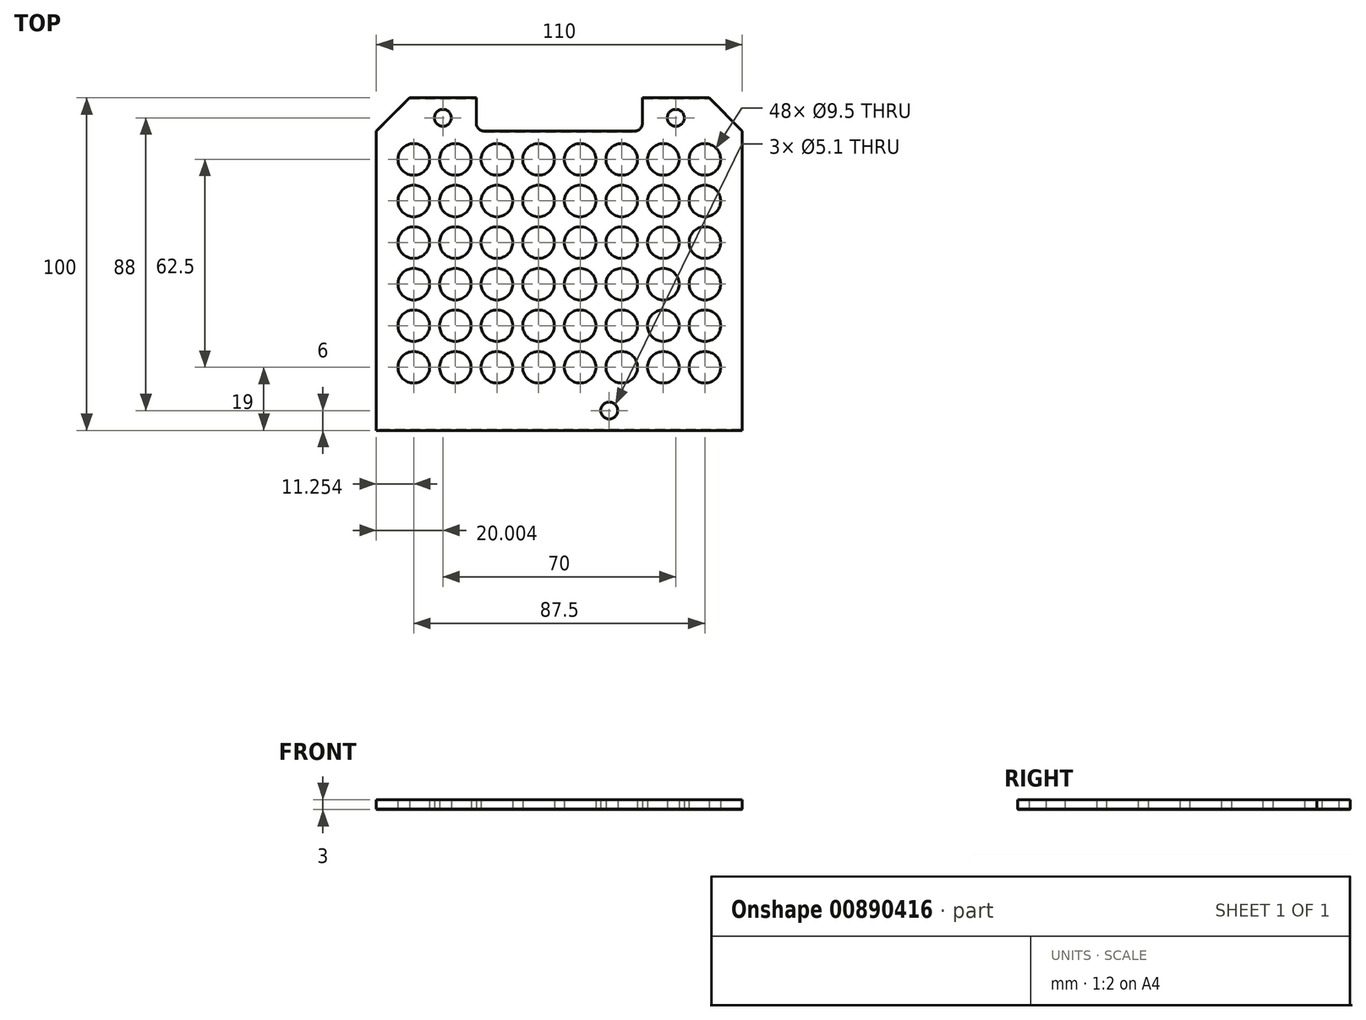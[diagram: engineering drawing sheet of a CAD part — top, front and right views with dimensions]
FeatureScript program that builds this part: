
annotation { "Feature Type Name" : "Feature", "Feature Type Description" : "" }
export const myFeature = defineFeature(function(context is Context, id is Id, definition is map)
    precondition{}
    {
        {
            var Q0;
            Q0=qCreatedBy(makeId("Top.planeOp"),FACE);
            var sketch = newSketch(context, id + "F0", { "sketchPlane" : qUnion([Q0])});
            skLineSegment(sketch, "E0", {"start": v(-42.4, 0) * mm, "end": v(67.6, 0) * mm});
            skLineSegment(sketch, "E1", {"start": v(-42.4, 100) * mm, "end": v(67.6, 100) * mm, "construction": true});
            skLineSegment(sketch, "E2", {"start": v(-42.4, 0) * mm, "end": v(-42.4, 100) * mm, "construction": true});
            skLineSegment(sketch, "E3", {"start": v(67.6, 0) * mm, "end": v(67.6, 100) * mm, "construction": true});
            skLineSegment(sketch, "E4", {"start": v(-12.4, 100) * mm, "end": v(-12.4, 90) * mm});
            skLineSegment(sketch, "E5", {"start": v(-12.4, 90) * mm, "end": v(37.6, 90) * mm});
            skLineSegment(sketch, "E6", {"start": v(37.6, 90) * mm, "end": v(37.6, 100) * mm});
            skLineSegment(sketch, "E7", {"start": v(-12.4, 100) * mm, "end": v(-32.4, 100) * mm});
            skLineSegment(sketch, "E8", {"start": v(-32.4, 100) * mm, "end": v(-42.4, 90) * mm});
            skLineSegment(sketch, "E9", {"start": v(-42.4, 90) * mm, "end": v(-42.4, 0) * mm});
            skLineSegment(sketch, "E10", {"start": v(37.6, 100) * mm, "end": v(57.6, 100) * mm});
            skLineSegment(sketch, "E11", {"start": v(57.6, 100) * mm, "end": v(67.6, 90) * mm});
            skLineSegment(sketch, "E12", {"start": v(67.6, 90) * mm, "end": v(67.6, 0) * mm});
            skLineSegment(sketch, "E13", {"start": v(-42.4, 19) * mm, "end": v(67.6, 19) * mm, "construction": true});
            skCircle(sketch, "E14", {"center": v(-31.16, 19) * mm, "radius": 4.75 * mm});
            skCircle(sketch, "E15.0.1.0", {"center": v(-31.16, 31.5) * mm, "radius": 4.75 * mm});
            skCircle(sketch, "E15.0.2.0", {"center": v(-31.16, 44) * mm, "radius": 4.75 * mm});
            skCircle(sketch, "E15.0.3.0", {"center": v(-31.16, 56.5) * mm, "radius": 4.75 * mm});
            skCircle(sketch, "E15.0.4.0", {"center": v(-31.16, 69) * mm, "radius": 4.75 * mm});
            skCircle(sketch, "E15.0.5.0", {"center": v(-31.16, 81.5) * mm, "radius": 4.75 * mm});
            skCircle(sketch, "E15.1.0.0", {"center": v(-18.66, 19) * mm, "radius": 4.75 * mm});
            skCircle(sketch, "E15.1.1.0", {"center": v(-18.66, 31.5) * mm, "radius": 4.75 * mm});
            skCircle(sketch, "E15.1.2.0", {"center": v(-18.66, 44) * mm, "radius": 4.75 * mm});
            skCircle(sketch, "E15.1.3.0", {"center": v(-18.66, 56.5) * mm, "radius": 4.75 * mm});
            skCircle(sketch, "E15.1.4.0", {"center": v(-18.66, 69) * mm, "radius": 4.75 * mm});
            skCircle(sketch, "E15.1.5.0", {"center": v(-18.66, 81.5) * mm, "radius": 4.75 * mm});
            skCircle(sketch, "E15.2.0.0", {"center": v(-6.16, 19) * mm, "radius": 4.75 * mm});
            skCircle(sketch, "E15.2.1.0", {"center": v(-6.16, 31.5) * mm, "radius": 4.75 * mm});
            skCircle(sketch, "E15.2.2.0", {"center": v(-6.16, 44) * mm, "radius": 4.75 * mm});
            skCircle(sketch, "E15.2.3.0", {"center": v(-6.16, 56.5) * mm, "radius": 4.75 * mm});
            skCircle(sketch, "E15.2.4.0", {"center": v(-6.16, 69) * mm, "radius": 4.75 * mm});
            skCircle(sketch, "E15.2.5.0", {"center": v(-6.16, 81.5) * mm, "radius": 4.75 * mm});
            skCircle(sketch, "E15.3.0.0", {"center": v(6.34, 19) * mm, "radius": 4.75 * mm});
            skCircle(sketch, "E15.3.1.0", {"center": v(6.34, 31.5) * mm, "radius": 4.75 * mm});
            skCircle(sketch, "E15.3.2.0", {"center": v(6.34, 44) * mm, "radius": 4.75 * mm});
            skCircle(sketch, "E15.3.3.0", {"center": v(6.34, 56.5) * mm, "radius": 4.75 * mm});
            skCircle(sketch, "E15.3.4.0", {"center": v(6.34, 69) * mm, "radius": 4.75 * mm});
            skCircle(sketch, "E15.3.5.0", {"center": v(6.34, 81.5) * mm, "radius": 4.75 * mm});
            skCircle(sketch, "E15.4.0.0", {"center": v(18.84, 19) * mm, "radius": 4.75 * mm});
            skCircle(sketch, "E15.4.1.0", {"center": v(18.84, 31.5) * mm, "radius": 4.75 * mm});
            skCircle(sketch, "E15.4.2.0", {"center": v(18.84, 44) * mm, "radius": 4.75 * mm});
            skCircle(sketch, "E15.4.3.0", {"center": v(18.84, 56.5) * mm, "radius": 4.75 * mm});
            skCircle(sketch, "E15.4.4.0", {"center": v(18.84, 69) * mm, "radius": 4.75 * mm});
            skCircle(sketch, "E15.4.5.0", {"center": v(18.84, 81.5) * mm, "radius": 4.75 * mm});
            skCircle(sketch, "E15.5.0.0", {"center": v(31.34, 19) * mm, "radius": 4.75 * mm});
            skCircle(sketch, "E15.5.1.0", {"center": v(31.34, 31.5) * mm, "radius": 4.75 * mm});
            skCircle(sketch, "E15.5.2.0", {"center": v(31.34, 44) * mm, "radius": 4.75 * mm});
            skCircle(sketch, "E15.5.3.0", {"center": v(31.34, 56.5) * mm, "radius": 4.75 * mm});
            skCircle(sketch, "E15.5.4.0", {"center": v(31.34, 69) * mm, "radius": 4.75 * mm});
            skCircle(sketch, "E15.5.5.0", {"center": v(31.34, 81.5) * mm, "radius": 4.75 * mm});
            skCircle(sketch, "E15.6.0.0", {"center": v(43.84, 19) * mm, "radius": 4.75 * mm});
            skCircle(sketch, "E15.6.1.0", {"center": v(43.84, 31.5) * mm, "radius": 4.75 * mm});
            skCircle(sketch, "E15.6.2.0", {"center": v(43.84, 44) * mm, "radius": 4.75 * mm});
            skCircle(sketch, "E15.6.3.0", {"center": v(43.84, 56.5) * mm, "radius": 4.75 * mm});
            skCircle(sketch, "E15.6.4.0", {"center": v(43.84, 69) * mm, "radius": 4.75 * mm});
            skCircle(sketch, "E15.6.5.0", {"center": v(43.84, 81.5) * mm, "radius": 4.75 * mm});
            skCircle(sketch, "E15.7.0.0", {"center": v(56.34, 19) * mm, "radius": 4.75 * mm});
            skCircle(sketch, "E15.7.1.0", {"center": v(56.34, 31.5) * mm, "radius": 4.75 * mm});
            skCircle(sketch, "E15.7.2.0", {"center": v(56.34, 44) * mm, "radius": 4.75 * mm});
            skCircle(sketch, "E15.7.3.0", {"center": v(56.34, 56.5) * mm, "radius": 4.75 * mm});
            skCircle(sketch, "E15.7.4.0", {"center": v(56.34, 69) * mm, "radius": 4.75 * mm});
            skCircle(sketch, "E15.7.5.0", {"center": v(56.34, 81.5) * mm, "radius": 4.75 * mm});
            skLineSegment(sketch, "E15.direction1", {"start": v(-31.16, 19) * mm, "end": v(-18.66, 19) * mm, "construction": true});
            skLineSegment(sketch, "E15.direction2", {"start": v(-31.16, 19) * mm, "end": v(-31.16, 31.5) * mm, "construction": true});
            skCircle(sketch, "E16", {"center": v(27.6, 6) * mm, "radius": 2.55 * mm});
            skCircle(sketch, "E17", {"center": v(47.6, 94) * mm, "radius": 2.55 * mm});
            skCircle(sketch, "E18", {"center": v(-22.4, 94) * mm, "radius": 2.55 * mm});
            skSolve(sketch);
        }
        {
            var Q0;
            Q0 = qSketchRegion(id + "F0", true);
            extrude(context, id + "F1", {"entities" : qUnion([Q0]), "depth" : 3 * mm, "offsetDistance" : 25 * mm});
        }
        {
            var Q0;
            Q0=makeQuery(id+"F1.opExtrude","SWEPT_EDGE",EDGE,{"disambiguationData":[OSD([sQuery(id+"F0.wireOp",EDGE,"E4"),sQuery(id+"F0.wireOp",EDGE,"E5")])]});
            var Q1;
            Q1=makeQuery(id+"F1.opExtrude","SWEPT_EDGE",EDGE,{"disambiguationData":[OSD([sQuery(id+"F0.wireOp",EDGE,"E5"),sQuery(id+"F0.wireOp",EDGE,"E6")])]});
            fillet(context, id + "F2", {"entities" : qUnion([Q0, Q1]), "radius" : 2.5 * mm, "tangentPropagation" : true, "allowEdgeOverflow" : false});
        }
        {
            var Q0;
            Q0=makeQuery(id+"F1.opExtrude","CAP_EDGE",EDGE,{"disambiguationData":[OSD([sQuery(id+"F0.wireOp",EDGE,"E0")])],"isStart":true});
            var Q1;
            Q1=makeQuery(id+"F1.opExtrude","CAP_EDGE",EDGE,{"disambiguationData":[OSD([sQuery(id+"F0.wireOp",EDGE,"E12")])],"isStart":true});
            var Q2;
            Q2=makeQuery(id+"F1.opExtrude","CAP_EDGE",EDGE,{"disambiguationData":[OSD([sQuery(id+"F0.wireOp",EDGE,"E9")])],"isStart":true});
            var Q3;
            Q3=makeQuery(id+"F1.opExtrude","CAP_EDGE",EDGE,{"disambiguationData":[OSD([sQuery(id+"F0.wireOp",EDGE,"E11")])],"isStart":true});
            var Q4;
            Q4=makeQuery(id+"F1.opExtrude","CAP_EDGE",EDGE,{"disambiguationData":[OSD([sQuery(id+"F0.wireOp",EDGE,"E10")])],"isStart":true});
            var Q5;
            Q5=makeQuery(id+"F1.opExtrude","CAP_EDGE",EDGE,{"disambiguationData":[OSD([sQuery(id+"F0.wireOp",EDGE,"E4")])],"isStart":true});
            var Q6;
            Q6=makeQuery(id+"F1.opExtrude","CAP_EDGE",EDGE,{"disambiguationData":[OSD([sQuery(id+"F0.wireOp",EDGE,"E7")])],"isStart":true});
            var Q7;
            Q7=makeQuery(id+"F1.opExtrude","CAP_EDGE",EDGE,{"disambiguationData":[OSD([sQuery(id+"F0.wireOp",EDGE,"E8")])],"isStart":true});
            var Q8;
            {var subQ0=sQuery(id+"F0.wireOp",EDGE,"E5");var subQ1=sQuery(id+"F0.wireOp",EDGE,"E4");Q8=makeQuery(id+"F2.opFillet","BLEND_EDGE",EDGE,{"blendedFrom":[makeQuery(id+"F1.opExtrude","SWEPT_EDGE",EDGE,{"disambiguationData":[OSD([subQ1,subQ0])]}),makeQuery(id+"F1.opExtrude","CAP_FACE",FACE,{"disambiguationData":[OSD([sQuery(id+"F0.wireOp",EDGE,"E0"),subQ1,subQ0,sQuery(id+"F0.wireOp",EDGE,"E6"),sQuery(id+"F0.wireOp",EDGE,"E7"),sQuery(id+"F0.wireOp",EDGE,"E8"),sQuery(id+"F0.wireOp",EDGE,"E9"),sQuery(id+"F0.wireOp",EDGE,"E10"),sQuery(id+"F0.wireOp",EDGE,"E11"),sQuery(id+"F0.wireOp",EDGE,"E12"),sQuery(id+"F0.wireOp",EDGE,"E14"),sQuery(id+"F0.wireOp",EDGE,"E15.0.1.0"),sQuery(id+"F0.wireOp",EDGE,"E15.0.2.0"),sQuery(id+"F0.wireOp",EDGE,"E15.0.3.0"),sQuery(id+"F0.wireOp",EDGE,"E15.0.4.0"),sQuery(id+"F0.wireOp",EDGE,"E15.0.5.0"),sQuery(id+"F0.wireOp",EDGE,"E15.1.0.0"),sQuery(id+"F0.wireOp",EDGE,"E15.1.1.0"),sQuery(id+"F0.wireOp",EDGE,"E15.1.2.0"),sQuery(id+"F0.wireOp",EDGE,"E15.1.3.0"),sQuery(id+"F0.wireOp",EDGE,"E15.1.4.0"),sQuery(id+"F0.wireOp",EDGE,"E15.1.5.0"),sQuery(id+"F0.wireOp",EDGE,"E15.2.0.0"),sQuery(id+"F0.wireOp",EDGE,"E15.2.1.0"),sQuery(id+"F0.wireOp",EDGE,"E15.2.2.0"),sQuery(id+"F0.wireOp",EDGE,"E15.2.3.0"),sQuery(id+"F0.wireOp",EDGE,"E15.2.4.0"),sQuery(id+"F0.wireOp",EDGE,"E15.2.5.0"),sQuery(id+"F0.wireOp",EDGE,"E15.3.0.0"),sQuery(id+"F0.wireOp",EDGE,"E15.3.1.0"),sQuery(id+"F0.wireOp",EDGE,"E15.3.2.0"),sQuery(id+"F0.wireOp",EDGE,"E15.3.3.0"),sQuery(id+"F0.wireOp",EDGE,"E15.3.4.0"),sQuery(id+"F0.wireOp",EDGE,"E15.3.5.0"),sQuery(id+"F0.wireOp",EDGE,"E15.4.0.0"),sQuery(id+"F0.wireOp",EDGE,"E15.4.1.0"),sQuery(id+"F0.wireOp",EDGE,"E15.4.2.0"),sQuery(id+"F0.wireOp",EDGE,"E15.4.3.0"),sQuery(id+"F0.wireOp",EDGE,"E15.4.4.0"),sQuery(id+"F0.wireOp",EDGE,"E15.4.5.0"),sQuery(id+"F0.wireOp",EDGE,"E15.5.0.0"),sQuery(id+"F0.wireOp",EDGE,"E15.5.1.0"),sQuery(id+"F0.wireOp",EDGE,"E15.5.2.0"),sQuery(id+"F0.wireOp",EDGE,"E15.5.3.0"),sQuery(id+"F0.wireOp",EDGE,"E15.5.4.0"),sQuery(id+"F0.wireOp",EDGE,"E15.5.5.0"),sQuery(id+"F0.wireOp",EDGE,"E15.6.0.0"),sQuery(id+"F0.wireOp",EDGE,"E15.6.1.0"),sQuery(id+"F0.wireOp",EDGE,"E15.6.2.0"),sQuery(id+"F0.wireOp",EDGE,"E15.6.3.0"),sQuery(id+"F0.wireOp",EDGE,"E15.6.4.0"),sQuery(id+"F0.wireOp",EDGE,"E15.6.5.0"),sQuery(id+"F0.wireOp",EDGE,"E15.7.0.0"),sQuery(id+"F0.wireOp",EDGE,"E15.7.1.0"),sQuery(id+"F0.wireOp",EDGE,"E15.7.2.0"),sQuery(id+"F0.wireOp",EDGE,"E15.7.3.0"),sQuery(id+"F0.wireOp",EDGE,"E15.7.4.0"),sQuery(id+"F0.wireOp",EDGE,"E15.7.5.0"),sQuery(id+"F0.wireOp",EDGE,"E16"),sQuery(id+"F0.wireOp",EDGE,"E17"),sQuery(id+"F0.wireOp",EDGE,"E18")])],"isStart":true})],"blendedInto":[makeQuery(id+"F1.opExtrude","CAP_FACE",FACE,{"disambiguationData":[OSD([sQuery(id+"F0.wireOp",EDGE,"E0"),subQ1,subQ0,sQuery(id+"F0.wireOp",EDGE,"E6"),sQuery(id+"F0.wireOp",EDGE,"E7"),sQuery(id+"F0.wireOp",EDGE,"E8"),sQuery(id+"F0.wireOp",EDGE,"E9"),sQuery(id+"F0.wireOp",EDGE,"E10"),sQuery(id+"F0.wireOp",EDGE,"E11"),sQuery(id+"F0.wireOp",EDGE,"E12"),sQuery(id+"F0.wireOp",EDGE,"E14"),sQuery(id+"F0.wireOp",EDGE,"E15.0.1.0"),sQuery(id+"F0.wireOp",EDGE,"E15.0.2.0"),sQuery(id+"F0.wireOp",EDGE,"E15.0.3.0"),sQuery(id+"F0.wireOp",EDGE,"E15.0.4.0"),sQuery(id+"F0.wireOp",EDGE,"E15.0.5.0"),sQuery(id+"F0.wireOp",EDGE,"E15.1.0.0"),sQuery(id+"F0.wireOp",EDGE,"E15.1.1.0"),sQuery(id+"F0.wireOp",EDGE,"E15.1.2.0"),sQuery(id+"F0.wireOp",EDGE,"E15.1.3.0"),sQuery(id+"F0.wireOp",EDGE,"E15.1.4.0"),sQuery(id+"F0.wireOp",EDGE,"E15.1.5.0"),sQuery(id+"F0.wireOp",EDGE,"E15.2.0.0"),sQuery(id+"F0.wireOp",EDGE,"E15.2.1.0"),sQuery(id+"F0.wireOp",EDGE,"E15.2.2.0"),sQuery(id+"F0.wireOp",EDGE,"E15.2.3.0"),sQuery(id+"F0.wireOp",EDGE,"E15.2.4.0"),sQuery(id+"F0.wireOp",EDGE,"E15.2.5.0"),sQuery(id+"F0.wireOp",EDGE,"E15.3.0.0"),sQuery(id+"F0.wireOp",EDGE,"E15.3.1.0"),sQuery(id+"F0.wireOp",EDGE,"E15.3.2.0"),sQuery(id+"F0.wireOp",EDGE,"E15.3.3.0"),sQuery(id+"F0.wireOp",EDGE,"E15.3.4.0"),sQuery(id+"F0.wireOp",EDGE,"E15.3.5.0"),sQuery(id+"F0.wireOp",EDGE,"E15.4.0.0"),sQuery(id+"F0.wireOp",EDGE,"E15.4.1.0"),sQuery(id+"F0.wireOp",EDGE,"E15.4.2.0"),sQuery(id+"F0.wireOp",EDGE,"E15.4.3.0"),sQuery(id+"F0.wireOp",EDGE,"E15.4.4.0"),sQuery(id+"F0.wireOp",EDGE,"E15.4.5.0"),sQuery(id+"F0.wireOp",EDGE,"E15.5.0.0"),sQuery(id+"F0.wireOp",EDGE,"E15.5.1.0"),sQuery(id+"F0.wireOp",EDGE,"E15.5.2.0"),sQuery(id+"F0.wireOp",EDGE,"E15.5.3.0"),sQuery(id+"F0.wireOp",EDGE,"E15.5.4.0"),sQuery(id+"F0.wireOp",EDGE,"E15.5.5.0"),sQuery(id+"F0.wireOp",EDGE,"E15.6.0.0"),sQuery(id+"F0.wireOp",EDGE,"E15.6.1.0"),sQuery(id+"F0.wireOp",EDGE,"E15.6.2.0"),sQuery(id+"F0.wireOp",EDGE,"E15.6.3.0"),sQuery(id+"F0.wireOp",EDGE,"E15.6.4.0"),sQuery(id+"F0.wireOp",EDGE,"E15.6.5.0"),sQuery(id+"F0.wireOp",EDGE,"E15.7.0.0"),sQuery(id+"F0.wireOp",EDGE,"E15.7.1.0"),sQuery(id+"F0.wireOp",EDGE,"E15.7.2.0"),sQuery(id+"F0.wireOp",EDGE,"E15.7.3.0"),sQuery(id+"F0.wireOp",EDGE,"E15.7.4.0"),sQuery(id+"F0.wireOp",EDGE,"E15.7.5.0"),sQuery(id+"F0.wireOp",EDGE,"E16"),sQuery(id+"F0.wireOp",EDGE,"E17"),sQuery(id+"F0.wireOp",EDGE,"E18")])],"isStart":true})]});}
            var Q9;
            {var subQ0=sQuery(id+"F0.wireOp",EDGE,"E6");var subQ1=sQuery(id+"F0.wireOp",EDGE,"E5");Q9=makeQuery(id+"F2.opFillet","BLEND_EDGE",EDGE,{"blendedFrom":[makeQuery(id+"F1.opExtrude","SWEPT_EDGE",EDGE,{"disambiguationData":[OSD([subQ1,subQ0])]}),makeQuery(id+"F1.opExtrude","CAP_FACE",FACE,{"disambiguationData":[OSD([sQuery(id+"F0.wireOp",EDGE,"E0"),sQuery(id+"F0.wireOp",EDGE,"E4"),subQ1,subQ0,sQuery(id+"F0.wireOp",EDGE,"E7"),sQuery(id+"F0.wireOp",EDGE,"E8"),sQuery(id+"F0.wireOp",EDGE,"E9"),sQuery(id+"F0.wireOp",EDGE,"E10"),sQuery(id+"F0.wireOp",EDGE,"E11"),sQuery(id+"F0.wireOp",EDGE,"E12"),sQuery(id+"F0.wireOp",EDGE,"E14"),sQuery(id+"F0.wireOp",EDGE,"E15.0.1.0"),sQuery(id+"F0.wireOp",EDGE,"E15.0.2.0"),sQuery(id+"F0.wireOp",EDGE,"E15.0.3.0"),sQuery(id+"F0.wireOp",EDGE,"E15.0.4.0"),sQuery(id+"F0.wireOp",EDGE,"E15.0.5.0"),sQuery(id+"F0.wireOp",EDGE,"E15.1.0.0"),sQuery(id+"F0.wireOp",EDGE,"E15.1.1.0"),sQuery(id+"F0.wireOp",EDGE,"E15.1.2.0"),sQuery(id+"F0.wireOp",EDGE,"E15.1.3.0"),sQuery(id+"F0.wireOp",EDGE,"E15.1.4.0"),sQuery(id+"F0.wireOp",EDGE,"E15.1.5.0"),sQuery(id+"F0.wireOp",EDGE,"E15.2.0.0"),sQuery(id+"F0.wireOp",EDGE,"E15.2.1.0"),sQuery(id+"F0.wireOp",EDGE,"E15.2.2.0"),sQuery(id+"F0.wireOp",EDGE,"E15.2.3.0"),sQuery(id+"F0.wireOp",EDGE,"E15.2.4.0"),sQuery(id+"F0.wireOp",EDGE,"E15.2.5.0"),sQuery(id+"F0.wireOp",EDGE,"E15.3.0.0"),sQuery(id+"F0.wireOp",EDGE,"E15.3.1.0"),sQuery(id+"F0.wireOp",EDGE,"E15.3.2.0"),sQuery(id+"F0.wireOp",EDGE,"E15.3.3.0"),sQuery(id+"F0.wireOp",EDGE,"E15.3.4.0"),sQuery(id+"F0.wireOp",EDGE,"E15.3.5.0"),sQuery(id+"F0.wireOp",EDGE,"E15.4.0.0"),sQuery(id+"F0.wireOp",EDGE,"E15.4.1.0"),sQuery(id+"F0.wireOp",EDGE,"E15.4.2.0"),sQuery(id+"F0.wireOp",EDGE,"E15.4.3.0"),sQuery(id+"F0.wireOp",EDGE,"E15.4.4.0"),sQuery(id+"F0.wireOp",EDGE,"E15.4.5.0"),sQuery(id+"F0.wireOp",EDGE,"E15.5.0.0"),sQuery(id+"F0.wireOp",EDGE,"E15.5.1.0"),sQuery(id+"F0.wireOp",EDGE,"E15.5.2.0"),sQuery(id+"F0.wireOp",EDGE,"E15.5.3.0"),sQuery(id+"F0.wireOp",EDGE,"E15.5.4.0"),sQuery(id+"F0.wireOp",EDGE,"E15.5.5.0"),sQuery(id+"F0.wireOp",EDGE,"E15.6.0.0"),sQuery(id+"F0.wireOp",EDGE,"E15.6.1.0"),sQuery(id+"F0.wireOp",EDGE,"E15.6.2.0"),sQuery(id+"F0.wireOp",EDGE,"E15.6.3.0"),sQuery(id+"F0.wireOp",EDGE,"E15.6.4.0"),sQuery(id+"F0.wireOp",EDGE,"E15.6.5.0"),sQuery(id+"F0.wireOp",EDGE,"E15.7.0.0"),sQuery(id+"F0.wireOp",EDGE,"E15.7.1.0"),sQuery(id+"F0.wireOp",EDGE,"E15.7.2.0"),sQuery(id+"F0.wireOp",EDGE,"E15.7.3.0"),sQuery(id+"F0.wireOp",EDGE,"E15.7.4.0"),sQuery(id+"F0.wireOp",EDGE,"E15.7.5.0"),sQuery(id+"F0.wireOp",EDGE,"E16"),sQuery(id+"F0.wireOp",EDGE,"E17"),sQuery(id+"F0.wireOp",EDGE,"E18")])],"isStart":true})],"blendedInto":[makeQuery(id+"F1.opExtrude","CAP_FACE",FACE,{"disambiguationData":[OSD([sQuery(id+"F0.wireOp",EDGE,"E0"),sQuery(id+"F0.wireOp",EDGE,"E4"),subQ1,subQ0,sQuery(id+"F0.wireOp",EDGE,"E7"),sQuery(id+"F0.wireOp",EDGE,"E8"),sQuery(id+"F0.wireOp",EDGE,"E9"),sQuery(id+"F0.wireOp",EDGE,"E10"),sQuery(id+"F0.wireOp",EDGE,"E11"),sQuery(id+"F0.wireOp",EDGE,"E12"),sQuery(id+"F0.wireOp",EDGE,"E14"),sQuery(id+"F0.wireOp",EDGE,"E15.0.1.0"),sQuery(id+"F0.wireOp",EDGE,"E15.0.2.0"),sQuery(id+"F0.wireOp",EDGE,"E15.0.3.0"),sQuery(id+"F0.wireOp",EDGE,"E15.0.4.0"),sQuery(id+"F0.wireOp",EDGE,"E15.0.5.0"),sQuery(id+"F0.wireOp",EDGE,"E15.1.0.0"),sQuery(id+"F0.wireOp",EDGE,"E15.1.1.0"),sQuery(id+"F0.wireOp",EDGE,"E15.1.2.0"),sQuery(id+"F0.wireOp",EDGE,"E15.1.3.0"),sQuery(id+"F0.wireOp",EDGE,"E15.1.4.0"),sQuery(id+"F0.wireOp",EDGE,"E15.1.5.0"),sQuery(id+"F0.wireOp",EDGE,"E15.2.0.0"),sQuery(id+"F0.wireOp",EDGE,"E15.2.1.0"),sQuery(id+"F0.wireOp",EDGE,"E15.2.2.0"),sQuery(id+"F0.wireOp",EDGE,"E15.2.3.0"),sQuery(id+"F0.wireOp",EDGE,"E15.2.4.0"),sQuery(id+"F0.wireOp",EDGE,"E15.2.5.0"),sQuery(id+"F0.wireOp",EDGE,"E15.3.0.0"),sQuery(id+"F0.wireOp",EDGE,"E15.3.1.0"),sQuery(id+"F0.wireOp",EDGE,"E15.3.2.0"),sQuery(id+"F0.wireOp",EDGE,"E15.3.3.0"),sQuery(id+"F0.wireOp",EDGE,"E15.3.4.0"),sQuery(id+"F0.wireOp",EDGE,"E15.3.5.0"),sQuery(id+"F0.wireOp",EDGE,"E15.4.0.0"),sQuery(id+"F0.wireOp",EDGE,"E15.4.1.0"),sQuery(id+"F0.wireOp",EDGE,"E15.4.2.0"),sQuery(id+"F0.wireOp",EDGE,"E15.4.3.0"),sQuery(id+"F0.wireOp",EDGE,"E15.4.4.0"),sQuery(id+"F0.wireOp",EDGE,"E15.4.5.0"),sQuery(id+"F0.wireOp",EDGE,"E15.5.0.0"),sQuery(id+"F0.wireOp",EDGE,"E15.5.1.0"),sQuery(id+"F0.wireOp",EDGE,"E15.5.2.0"),sQuery(id+"F0.wireOp",EDGE,"E15.5.3.0"),sQuery(id+"F0.wireOp",EDGE,"E15.5.4.0"),sQuery(id+"F0.wireOp",EDGE,"E15.5.5.0"),sQuery(id+"F0.wireOp",EDGE,"E15.6.0.0"),sQuery(id+"F0.wireOp",EDGE,"E15.6.1.0"),sQuery(id+"F0.wireOp",EDGE,"E15.6.2.0"),sQuery(id+"F0.wireOp",EDGE,"E15.6.3.0"),sQuery(id+"F0.wireOp",EDGE,"E15.6.4.0"),sQuery(id+"F0.wireOp",EDGE,"E15.6.5.0"),sQuery(id+"F0.wireOp",EDGE,"E15.7.0.0"),sQuery(id+"F0.wireOp",EDGE,"E15.7.1.0"),sQuery(id+"F0.wireOp",EDGE,"E15.7.2.0"),sQuery(id+"F0.wireOp",EDGE,"E15.7.3.0"),sQuery(id+"F0.wireOp",EDGE,"E15.7.4.0"),sQuery(id+"F0.wireOp",EDGE,"E15.7.5.0"),sQuery(id+"F0.wireOp",EDGE,"E16"),sQuery(id+"F0.wireOp",EDGE,"E17"),sQuery(id+"F0.wireOp",EDGE,"E18")])],"isStart":true})]});}
            var Q10;
            Q10=makeQuery(id+"F1.opExtrude","CAP_EDGE",EDGE,{"disambiguationData":[OSD([sQuery(id+"F0.wireOp",EDGE,"E6")])],"isStart":true});
            var Q11;
            Q11=makeQuery(id+"F1.opExtrude","CAP_EDGE",EDGE,{"disambiguationData":[OSD([sQuery(id+"F0.wireOp",EDGE,"E5")])],"isStart":true});
            chamfer(context, id + "F3", {"entities" : qUnion([Q0, Q1, Q2, Q3, Q4, Q5, Q6, Q7, Q8, Q9, Q10, Q11]), "width" : 0.2 * mm, "tangentPropagation" : true});
        }
    });
